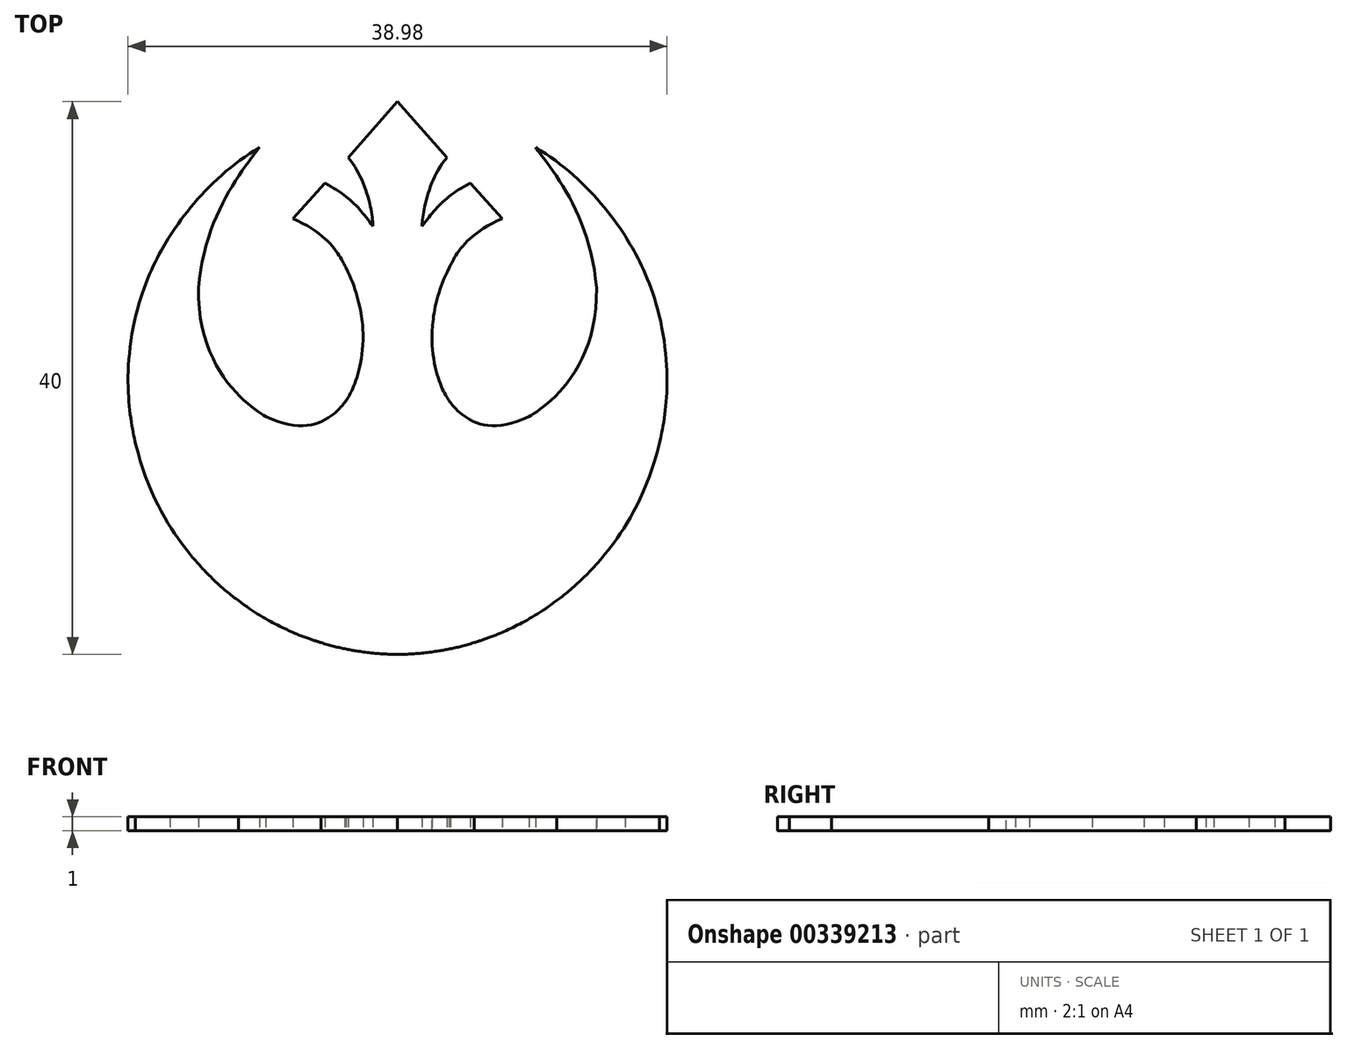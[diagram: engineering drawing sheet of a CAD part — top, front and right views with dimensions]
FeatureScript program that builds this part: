
annotation { "Feature Type Name" : "Feature", "Feature Type Description" : "" }
export const myFeature = defineFeature(function(context is Context, id is Id, definition is map)
    precondition{}
    {
        {
            var Q0;
            Q0=qCreatedBy(makeId("Top.planeOp"),FACE);
            var sketch = newSketch(context, id + "F0", { "sketchPlane" : qUnion([Q0])});
            skPoint(sketch, "E0.centerSnap0", {"position": v(-20.5, 0) * mm});
            skPoint(sketch, "E0.centerSnap1", {"position": v(0, 20.5) * mm});
            skPoint(sketch, "E1.11.internal.snap0", {"position": v(20.5, 0) * mm});
            skLineSegment(sketch, "E2", {"start": v(0, 20.04) * mm, "end": v(-3.58, 16) * mm});
            skLineSegment(sketch, "E3", {"start": v(-5.25, 14.14) * mm, "end": v(-7.58, 11.58) * mm});
            skFitSpline(sketch, "E4", {"points": [v(-3.58, 16) * mm, v(-1.78, 11.03) * mm], "startDerivative": vector(4.1, -4.8) * mm, "endDerivative": vector(0.1, -2.95) * mm});
            skFitSpline(sketch, "E5", {"points": [v(-1.78, 11.03) * mm, v(-5.25, 14.14) * mm], "startDerivative": vector(-2.9, 3.85) * mm, "endDerivative": vector(-5.37, 2.82) * mm});
            skFitSpline(sketch, "E6", {"points": [v(-7.58, 11.58) * mm, v(-3.73, 8) * mm], "startDerivative": vector(8.98, -3.93) * mm, "endDerivative": vector(0.87, -1.5) * mm});
            skFitSpline(sketch, "E7", {"points": [v(-3.73, 8) * mm, v(-2.5, 2.8) * mm], "startDerivative": vector(3.09, -6) * mm, "endDerivative": vector(-0.14, -3.55) * mm});
            skFitSpline(sketch, "E8", {"points": [v(-2.5, 2.8) * mm, v(-3.82, -1.75) * mm], "startDerivative": vector(-0.22, -8.63) * mm, "endDerivative": vector(-0.46, -0.74) * mm});
            skFitSpline(sketch, "E9", {"points": [v(-3.82, -1.75) * mm, v(-9.53, -2.74) * mm], "startDerivative": vector(-1.64, -1.97) * mm, "endDerivative": vector(-10.35, 5.24) * mm});
            skFitSpline(sketch, "E10", {"points": [v(-9.53, -2.74) * mm, v(-14.4, 6.54) * mm], "startDerivative": vector(-3.32, 1.82) * mm, "endDerivative": vector(0.41, 17.84) * mm});
            skFitSpline(sketch, "E11", {"points": [v(-14.4, 6.54) * mm, v(-9.98, 16.73) * mm], "startDerivative": vector(1.23, 15.51) * mm, "endDerivative": vector(4.08, 5.45) * mm});
            skPoint(sketch, "E12.1.internal.snap0", {"position": v(0, -20.5) * mm});
            skFitSpline(sketch, "E13", {"points": [v(-9.98, 16.73) * mm, v(-16.46, 10.33) * mm], "startDerivative": vector(-8.6, -5.07) * mm, "endDerivative": vector(-4.24, -6.58) * mm});
            skFitSpline(sketch, "E14", {"points": [v(-16.46, 10.33) * mm, v(-19.28, 2.76) * mm], "startDerivative": vector(-2.72, -4.38) * mm, "endDerivative": vector(-1.65, -11.09) * mm});
            skFitSpline(sketch, "E15", {"points": [v(-19.28, 2.76) * mm, v(-18.95, -4.7) * mm], "startDerivative": vector(-1.54, -11.03) * mm, "endDerivative": vector(0.88, -4.1) * mm});
            skFitSpline(sketch, "E16", {"points": [v(-18.95, -4.7) * mm, v(-14.2, -13.64) * mm], "startDerivative": vector(3.55, -14.93) * mm, "endDerivative": vector(2.81, -3.1) * mm});
            skFitSpline(sketch, "E17", {"points": [v(-14.2, -13.64) * mm, v(-11.5, -16.07) * mm], "startDerivative": vector(2.4, -2.63) * mm, "endDerivative": vector(2.16, -1.42) * mm});
            skFitSpline(sketch, "E18", {"points": [v(-11.5, -16.07) * mm, v(-7.43, -18.42) * mm], "startDerivative": vector(4.6, -3.54) * mm, "endDerivative": vector(3.17, -1.37) * mm});
            skFitSpline(sketch, "E19", {"points": [v(-7.43, -18.42) * mm, v(-5.54, -19.1) * mm], "startDerivative": vector(2.27, -0.98) * mm, "endDerivative": vector(1.26, -0.39) * mm});
            skFitSpline(sketch, "E20", {"points": [v(-5.54, -19.1) * mm, v(-2.98, -19.7) * mm], "startDerivative": vector(2.82, -0.92) * mm, "endDerivative": vector(2.25, -0.37) * mm});
            skFitSpline(sketch, "E21", {"points": [v(-2.98, -19.7) * mm, v(0, -19.96) * mm], "startDerivative": vector(2.88, -0.5) * mm, "endDerivative": vector(2.24, 0.03) * mm});
            skFitSpline(sketch, "E22.MirrorCS", {"points": [v(7.43, -18.42) * mm, v(5.54, -19.1) * mm], "startDerivative": vector(-2.27, -0.98) * mm, "endDerivative": vector(-1.26, -0.39) * mm});
            skFitSpline(sketch, "E23.MirrorCS", {"points": [v(14.2, -13.64) * mm, v(11.5, -16.07) * mm], "startDerivative": vector(-2.4, -2.63) * mm, "endDerivative": vector(-2.16, -1.42) * mm});
            skFitSpline(sketch, "E24.MirrorCS", {"points": [v(11.5, -16.07) * mm, v(7.43, -18.42) * mm], "startDerivative": vector(-4.6, -3.54) * mm, "endDerivative": vector(-3.17, -1.37) * mm});
            skFitSpline(sketch, "E25.MirrorCS", {"points": [v(9.98, 16.73) * mm, v(16.46, 10.33) * mm], "startDerivative": vector(8.6, -5.07) * mm, "endDerivative": vector(4.24, -6.58) * mm});
            skFitSpline(sketch, "E26.MirrorCS", {"points": [v(5.54, -19.1) * mm, v(2.98, -19.7) * mm], "startDerivative": vector(-2.82, -0.92) * mm, "endDerivative": vector(-2.25, -0.37) * mm});
            skFitSpline(sketch, "E27.MirrorCS", {"points": [v(1.78, 11.03) * mm, v(5.25, 14.14) * mm], "startDerivative": vector(2.9, 3.85) * mm, "endDerivative": vector(5.37, 2.82) * mm});
            skFitSpline(sketch, "E28.MirrorCS", {"points": [v(3.58, 16) * mm, v(1.78, 11.03) * mm], "startDerivative": vector(-4.1, -4.8) * mm, "endDerivative": vector(-0.1, -2.95) * mm});
            skFitSpline(sketch, "E29.MirrorCS", {"points": [v(3.73, 8) * mm, v(2.5, 2.8) * mm], "startDerivative": vector(-3.09, -6) * mm, "endDerivative": vector(0.14, -3.55) * mm});
            skFitSpline(sketch, "E30.MirrorCS", {"points": [v(14.4, 6.54) * mm, v(9.98, 16.73) * mm], "startDerivative": vector(-1.23, 15.51) * mm, "endDerivative": vector(-4.08, 5.45) * mm});
            skFitSpline(sketch, "E31.MirrorCS", {"points": [v(16.46, 10.33) * mm, v(19.28, 2.76) * mm], "startDerivative": vector(2.72, -4.38) * mm, "endDerivative": vector(1.65, -11.09) * mm});
            skFitSpline(sketch, "E32.MirrorCS", {"points": [v(18.95, -4.7) * mm, v(14.2, -13.64) * mm], "startDerivative": vector(-3.55, -14.93) * mm, "endDerivative": vector(-2.81, -3.1) * mm});
            skFitSpline(sketch, "E33.MirrorCS", {"points": [v(19.28, 2.76) * mm, v(18.95, -4.7) * mm], "startDerivative": vector(1.54, -11.03) * mm, "endDerivative": vector(-0.88, -4.1) * mm});
            skFitSpline(sketch, "E34.MirrorCS", {"points": [v(7.58, 11.58) * mm, v(3.73, 8) * mm], "startDerivative": vector(-8.98, -3.93) * mm, "endDerivative": vector(-0.87, -1.5) * mm});
            skFitSpline(sketch, "E35.MirrorCS", {"points": [v(9.53, -2.74) * mm, v(14.4, 6.54) * mm], "startDerivative": vector(3.32, 1.82) * mm, "endDerivative": vector(-0.41, 17.84) * mm});
            skFitSpline(sketch, "E36.MirrorCS", {"points": [v(3.82, -1.75) * mm, v(9.53, -2.74) * mm], "startDerivative": vector(1.64, -1.97) * mm, "endDerivative": vector(10.35, 5.24) * mm});
            skLineSegment(sketch, "E37.MirrorCS", {"start": v(5.25, 14.14) * mm, "end": v(7.58, 11.58) * mm});
            skFitSpline(sketch, "E38.MirrorCS", {"points": [v(2.5, 2.8) * mm, v(3.82, -1.75) * mm], "startDerivative": vector(0.22, -8.63) * mm, "endDerivative": vector(0.46, -0.74) * mm});
            skLineSegment(sketch, "E39.MirrorCS", {"start": v(0, 20.04) * mm, "end": v(3.58, 16) * mm});
            skFitSpline(sketch, "E40.MirrorCS", {"points": [v(2.98, -19.7) * mm, v(0, -19.96) * mm], "startDerivative": vector(-2.88, -0.5) * mm, "endDerivative": vector(-2.24, 0.03) * mm});
            skSolve(sketch);
        }
        {
            var Q0;
            Q0=makeQuery(id+"F0.imprint","IMPRINT",FACE,{"disambiguationData":[TD([[makeQuery(id+"F0.imprint","IMPRINT",EDGE,{"derivedFrom":sQuery(id+"F0.wireOp",EDGE,"E2")}),1.0]])]});
            extrude(context, id + "F1", {"entities" : qUnion([Q0]), "depth" : 1 * mm});
        }
    });
